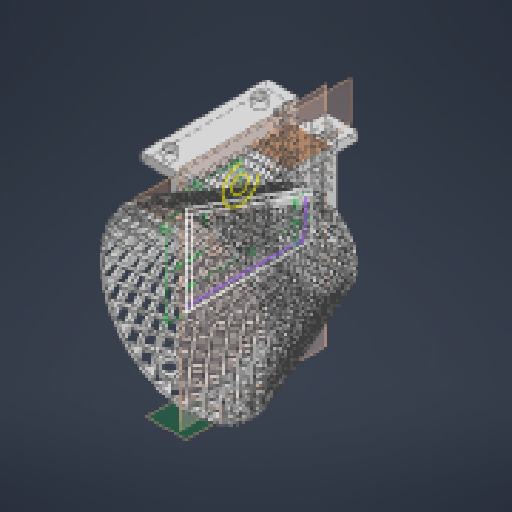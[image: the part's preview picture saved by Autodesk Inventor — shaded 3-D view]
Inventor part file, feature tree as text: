
AUTODESK INVENTOR PART (.ipt)
format: ipt  version: 2025 (Build 290162000, 162)  size: 3,740,160 bytes
history: native  units: mm
features: extrude x12, sketch x10, plane x9, other x8, reference x3, projected_geometry x2, pattern_circular x1, fillet x1
ambient origin geometry x8: Origin, YZ Plane, XZ Plane, XY Plane, X Axis, Y Axis, Z Axis, Center Point
bodies: Solid1 (feature_tree)
feature tree (46):
  plane  "Work Plane1"
  other  "hoop revolution"
  extrude  "net holes"  Depth=25.0mm
  pattern_circular  "Circular Pattern3"  Count=3  [1 undecoded]
  plane  "Work Plane15"
  extrude  "hoop slot"  TaperAngle=90.0deg  [1 undecoded]
  plane  "Work Plane10"
  extrude  "slot walls"  Depth=3.0mm
  plane  "Work Plane12"
  extrude  "arm holes"  Depth=1.0mm
  plane  "Work Plane11"
  sketch  "Sketch19"  dims[d392=1.0mm d393=1.0mm]
  plane  "Work Plane13"
  extrude  "mount holes extrusion"  Depth=1.0mm
  plane  "Work Plane16"
  extrude  "mounting holes and access holes"  Depth=1.0mm
  plane  "Work Plane18"
  extrude  "Extrusion13"  Depth=1.0mm
  plane  "Work Plane21"
  extrude  "back net reinforcement"  Depth=1.0mm
  fillet  "Fillet1"  Radius=1.0mm
  other  "middle plane for part"
  extrude  "Extrusion16"  Depth=1.0mm
  extrude  "Extrusion17"  Depth=10.0mm
  extrude  "Extrusion18"  Depth=10.0mm
  extrude  "Diameter Increase For Ball Clearance"  TaperAngle=0.0deg  [1 undecoded]
  reference  "Reference1"
  reference  "Reference2"
  reference  "Reference3"
  other  "best net sketch"
  projected_geometry  "Projected Loop3"
  sketch  "Sketch16"  dims[d387=1.0mm d388=1.0mm]
  sketch  "Sketch17"  dims[d389=1.0mm d390=1.0mm d391=1.0mm]
  projected_geometry  "Projected Loop4"
  sketch  "Sketch22"  dims[d394=1.0mm d395=1.0mm d396=1.0mm d397=0.0mm d398=0.0mm d399=3.572329mm d400=0.0mm d401=300.0mm d402=360.0deg d404=10.0mm d406=20.0mm d407=0.0mm d408=1.0mm d409=18.099mm d410=0.0mm d411=1.0mm d412=3.0mm d413=50.0mm d414=0.0mm d417=10.0mm d418=0.0mm d419=0.0mm d420=55.0mm d423=3.0mm d424=4.5mm d426=10.0mm d431=5.0mm d432=0.0mm d433=6.0mm d434=6.0mm d439=10.0mm d440=10.0mm d441=6.2mm d442=20.0mm d444=50.0mm d445=20.0mm d447=38.0mm d450=0.0mm d451=0.0mm d452=10.0mm d453=10.0mm d454=10.0mm d455=0.0mm d456=10.0mm d457=10.0mm d458=10.0mm d459=10.0mm d460=10.0mm d461=10.0mm d462=10.0mm d463=0.0mm d464=12.277724mm d465=12.278391mm d466=4.1mm d467=50.0mm d469=5.0mm d470=10.0mm d472=10.0mm d478=0.75mm d479=70.0mm d481=6.0mm d482=30.0mm d484=6.0mm d487=40.0mm d489=6.0mm d490=10.0mm d492=10.0mm d494=60.0mm d496=6.0mm d497=10.0mm d499=10.0mm d508=10.0mm d509=0.0mm d510=60.0mm d512=6.0mm d513=10.0mm d515=0.0mm d517=10.0mm d518=0.0mm d519=2.8mm d520=2.8mm d523=6.5mm d524=8.0mm d525=6.5mm d526=8.0mm d532=40.0mm d533=0.0mm d538=1.0mm d539=1.0mm d540=15.6mm d541=8.933823mm d542=1.0mm d543=0.0mm d544=0.0mm]
  sketch  "Sketch Rectangular Pattern1"  dims[d1=70.0mm d2=25.0mm d3=30.0mm]
  other  "net reinforcement"
  sketch  "Sketch Rectangular Pattern2"  dims[d5=3.0mm d6=90.0deg]
  sketch  "Sketch Rectangular Pattern3"  dims[d364=50.0mm d365=3.0mm]
  sketch  "Sketch Rectangular Pattern4"  dims[d380=1.0mm d382=1.0mm]
  sketch  "Sketch Rectangular Pattern5"  dims[d383=1.0mm d384=1.0mm]
  sketch  "Sketch Rectangular Pattern6"  dims[d385=1.0mm d386=1.0mm]
  other  "Diameter Increase"
  parser-record x1  (decoder bookkeeping rows leaked as tree rows — omitted from the tree; the rows remain in map.json)
  other  "BASKETBALL HOOP.iam"
  other  "BALL BEARING ARM:1"
note: 3 required parameter values undecoded (feature->parameter linkage not recoverable at this tier; creation-order binding heuristic only, values carry confidence <= 0.55)
note: 1 file-system path scrubbed to <path> (originals preserved in map.json)
